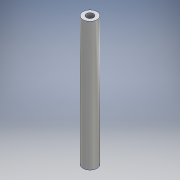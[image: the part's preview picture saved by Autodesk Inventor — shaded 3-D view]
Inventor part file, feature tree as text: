
AUTODESK INVENTOR PART (.ipt)
format: ipt  version: 2020.2 (Build 242310000, 310)  size: 100,352 bytes
history: native  units: mm
features: extrude x3, sketch x3, other x1
ambient origin geometry x8: Origin, YZ Plane, XZ Plane, XY Plane, X Axis, Y Axis, Z Axis, Center Point
bodies: Body1 (feature_tree)
feature tree (7):
  other  "ソリッド1"
  extrude  "押し出し1"  Depth=6.0mm
  extrude  "押し出し2"  Depth=55.0mm TaperAngle=0.0deg
  extrude  "押し出し3"  Depth=3.0mm
  sketch  "スケッチ1"
  sketch  "スケッチ2"
  sketch  "スケッチ3"
